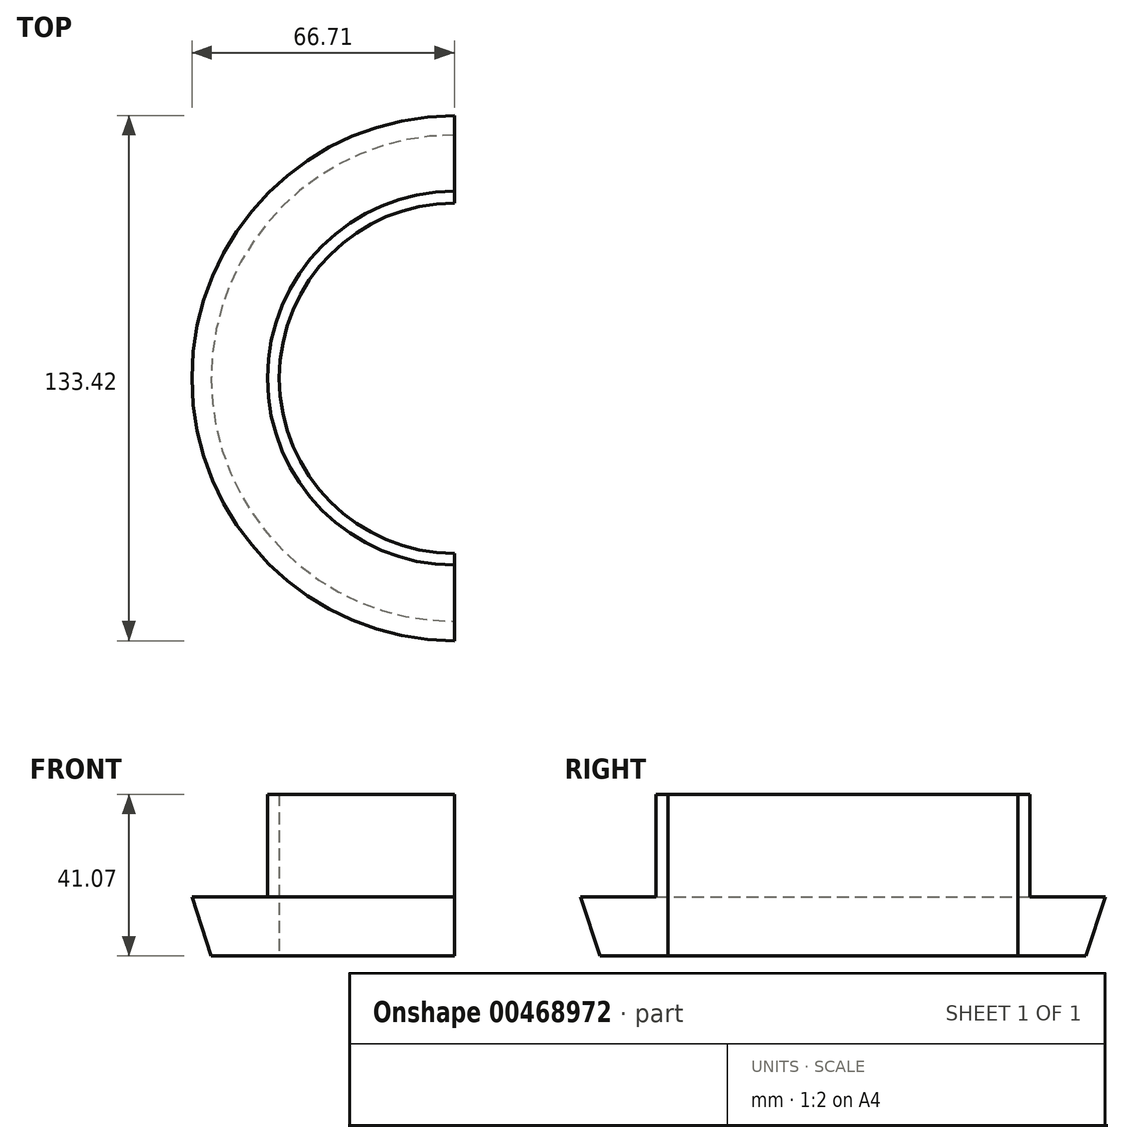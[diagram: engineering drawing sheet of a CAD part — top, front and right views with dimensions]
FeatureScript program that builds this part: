
annotation { "Feature Type Name" : "Feature", "Feature Type Description" : "" }
export const myFeature = defineFeature(function(context is Context, id is Id, definition is map)
    precondition{}
    {
        {
            var Q0;
            Q0=qCreatedBy(makeId("Front.planeOp"),FACE);
            var sketch = newSketch(context, id + "F0", { "sketchPlane" : qUnion([Q0])});
            skLineSegment(sketch, "E0", {"start": v(0, 0) * mm, "end": v(0, 90.51) * mm, "construction": true});
            skLineSegment(sketch, "E1", {"start": v(-61.77, 0) * mm, "end": v(-44.5, 0) * mm});
            skLineSegment(sketch, "E2", {"start": v(-44.5, 0) * mm, "end": v(-44.5, 41.07) * mm});
            skLineSegment(sketch, "E3", {"start": v(-44.5, 41.07) * mm, "end": v(-47.5, 41.07) * mm});
            skLineSegment(sketch, "E4", {"start": v(-47.5, 41.07) * mm, "end": v(-47.5, 15) * mm});
            skLineSegment(sketch, "E5", {"start": v(-47.5, 15) * mm, "end": v(-66.71, 15) * mm});
            skLineSegment(sketch, "E6", {"start": v(-66.71, 15) * mm, "end": v(-61.77, 0) * mm});
            skSolve(sketch);
        }
        {
            var Q0;
            Q0=makeQuery(id+"F0.imprint","IMPRINT",FACE,{"disambiguationData":[TD([[makeQuery(id+"F0.imprint","IMPRINT",EDGE,{"derivedFrom":sQuery(id+"F0.wireOp",EDGE,"E1")}),1.0]])]});
            var Q1;
            Q1=sQuery(id+"F0.wireOp",EDGE,"E0");
            revolve(context, id + "F1", {"surfaceOperationType" : NewSurfaceOperationType.NEW, "entities" : qUnion([Q0]), "axis" : qUnion([Q1]), "revolveType" : RevolveType.SYMMETRIC, "angle" : 180 * degree});
        }
    });
